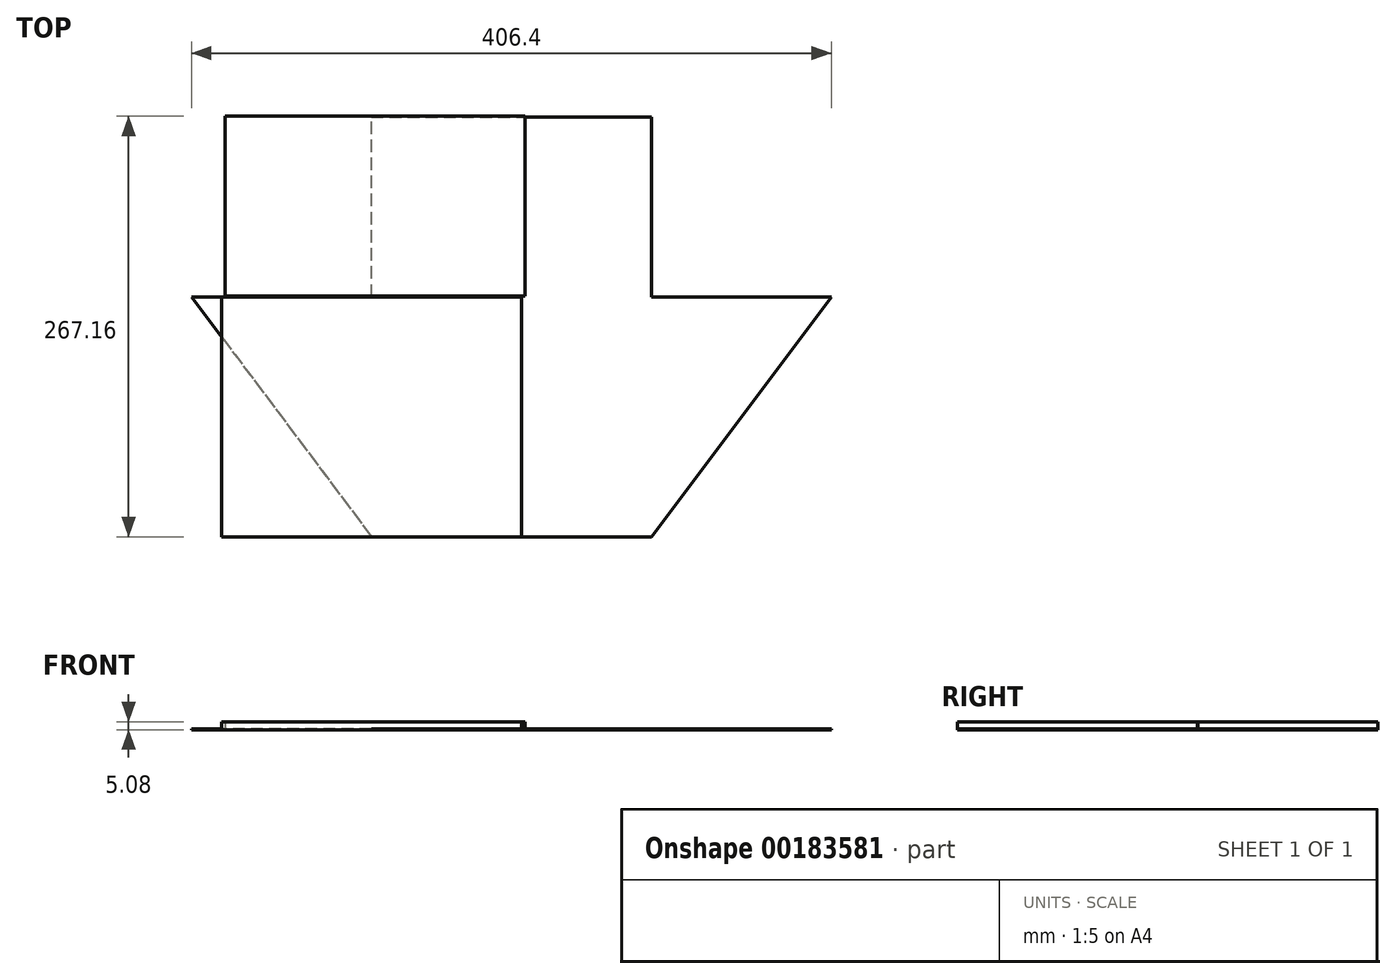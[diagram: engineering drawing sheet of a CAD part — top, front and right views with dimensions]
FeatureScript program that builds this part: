
annotation { "Feature Type Name" : "Feature", "Feature Type Description" : "" }
export const myFeature = defineFeature(function(context is Context, id is Id, definition is map)
    precondition{}
    {
        {
            var Q0;
            Q0=qCreatedBy(makeId("Top.planeOp"),FACE);
            var sketch = newSketch(context, id + "F0", { "sketchPlane" : qUnion([Q0])});
            skLineSegment(sketch, "E0.bottom", {"start": v(-93, 114.76) * mm, "end": v(97.5, 114.76) * mm});
            skLineSegment(sketch, "E0.top", {"start": v(-93, 0.46) * mm, "end": v(97.5, 0.46) * mm});
            skLineSegment(sketch, "E0.left", {"start": v(-93, 114.76) * mm, "end": v(-93, 0.46) * mm});
            skLineSegment(sketch, "E0.right", {"start": v(97.5, 114.76) * mm, "end": v(97.5, 0.46) * mm});
            skSolve(sketch);
        }
        {
            var Q0;
            Q0 = qSketchRegion(id + "F0", true);
            extrude(context, id + "F1", {"entities" : qUnion([Q0]), "depth" : 5.08 * mm});
        }
        {
            var Q0;
            Q0=qCreatedBy(makeId("Top.planeOp"),FACE);
            var sketch = newSketch(context, id + "F2", { "sketchPlane" : qUnion([Q0])});
            skLineSegment(sketch, "E1.bottom", {"start": v(95.25, 0) * mm, "end": v(-95.25, 0) * mm});
            skLineSegment(sketch, "E1.top", {"start": v(95.25, -152.4) * mm, "end": v(-95.25, -152.4) * mm});
            skLineSegment(sketch, "E1.left", {"start": v(95.25, 0) * mm, "end": v(95.25, -152.4) * mm});
            skLineSegment(sketch, "E1.right", {"start": v(-95.25, 0) * mm, "end": v(-95.25, -152.4) * mm});
            skPoint(sketch, "E1.middle", {"position": v(0, -76.2) * mm});
            skSolve(sketch);
        }
        {
            var Q0;
            Q0 = qSketchRegion(id + "F2", true);
            extrude(context, id + "F3", {"entities" : qUnion([Q0]), "depth" : 5.08 * mm});
        }
        {
            var Q0;
            Q0=qCreatedBy(makeId("Top.planeOp"),FACE);
            var sketch = newSketch(context, id + "F4", { "sketchPlane" : qUnion([Q0])});
            skLineSegment(sketch, "E2", {"start": v(0, 0) * mm, "end": v(0, 114.3) * mm});
            skLineSegment(sketch, "E3", {"start": v(0, 114.3) * mm, "end": v(177.8, 114.3) * mm});
            skLineSegment(sketch, "E4", {"start": v(177.8, 114.3) * mm, "end": v(177.8, 0) * mm});
            skLineSegment(sketch, "E5", {"start": v(177.8, 0) * mm, "end": v(292.1, 0) * mm});
            skLineSegment(sketch, "E6", {"start": v(177.8, 0) * mm, "end": v(177.8, -152.4) * mm});
            skLineSegment(sketch, "E7", {"start": v(177.8, -152.4) * mm, "end": v(0, -152.4) * mm});
            skLineSegment(sketch, "E8", {"start": v(0, -152.4) * mm, "end": v(0, 0) * mm});
            skLineSegment(sketch, "E9", {"start": v(0, 0) * mm, "end": v(-114.3, 0) * mm});
            skLineSegment(sketch, "E10", {"start": v(-114.3, 0) * mm, "end": v(0, -152.4) * mm});
            skLineSegment(sketch, "E11", {"start": v(177.8, -152.4) * mm, "end": v(292.1, 0) * mm});
            skSolve(sketch);
        }
        {
            var Q0;
            Q0 = qSketchRegion(id + "F4", true);
            extrude(context, id + "F5", {"entities" : qUnion([Q0]), "depth" : 0.5 * mm});
        }
    });
